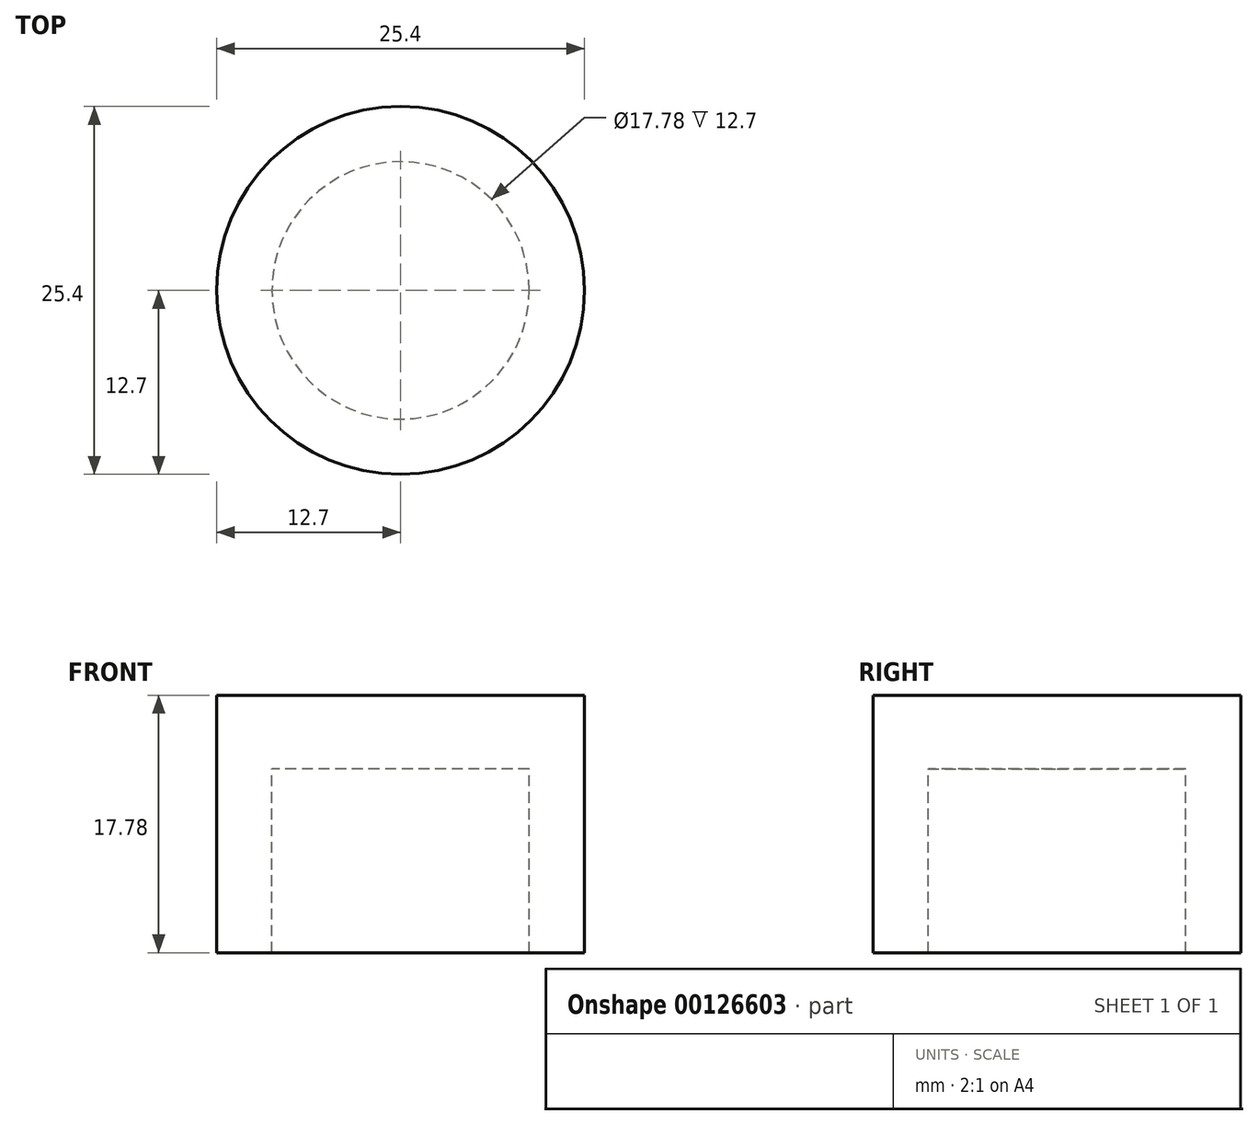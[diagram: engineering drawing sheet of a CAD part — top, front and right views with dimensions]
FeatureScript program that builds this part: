
annotation { "Feature Type Name" : "Feature", "Feature Type Description" : "" }
export const myFeature = defineFeature(function(context is Context, id is Id, definition is map)
    precondition{}
    {
        {
            var Q0;
            Q0=qCreatedBy(makeId("Top.planeOp"),FACE);
            var sketch = newSketch(context, id + "F0", { "sketchPlane" : qUnion([Q0])});
            skPoint(sketch, "E0", {"position": v(0, 0) * mm});
            skCircle(sketch, "E1", {"center": v(0, 0) * mm, "radius": 12.7 * mm});
            skPoint(sketch, "E2", {"position": v(12.7, 0) * mm});
            skPoint(sketch, "E3", {"position": v(8.9, 0) * mm});
            skCircle(sketch, "E4", {"center": v(0, 0) * mm, "radius": 8.9 * mm});
            skSolve(sketch);
        }
        {
            var Q0;
            Q0=makeQuery(id+"F0.imprint","IMPRINT",FACE,{"disambiguationData":[TD([[makeQuery(id+"F0.imprint","IMPRINT",EDGE,{"derivedFrom":sQuery(id+"F0.wireOp",EDGE,"E1")}),1.0]])]});
            extrude(context, id + "F2", {"entities" : qUnion([Q0]), "oppositeDirection" : true, "depth" : 12.7 * mm});
        }
        {
            var Q0;
            Q0=makeQuery(id+"F0.imprint","IMPRINT",FACE,{"disambiguationData":[TD([[makeQuery(id+"F0.imprint","IMPRINT",EDGE,{"derivedFrom":sQuery(id+"F0.wireOp",EDGE,"E1")}),1.0]])]});
            var Q1;
            Q1=makeQuery(id+"F0.imprint","IMPRINT",FACE,{"disambiguationData":[TD([[makeQuery(id+"F0.imprint","IMPRINT",EDGE,{"derivedFrom":sQuery(id+"F0.wireOp",EDGE,"E4")}),1.0]])]});
            extrude(context, id + "F3", {"entities" : qUnion([Q0, Q1]), "operationType" : NewBodyOperationType.ADD, "depth" : 5.08 * mm});
        }
        {
            var Q0;
            Q0=qCreatedBy(makeId("Front.planeOp"),FACE);
            cPlane(context, id + "F4", {"entities" : qUnion([Q0]), "cplaneType" : CPlaneType.OFFSET, "offset" : 12.7 * mm, "width" : 152.4 * mm, "height" : 152.4 * mm});
        }
    });
